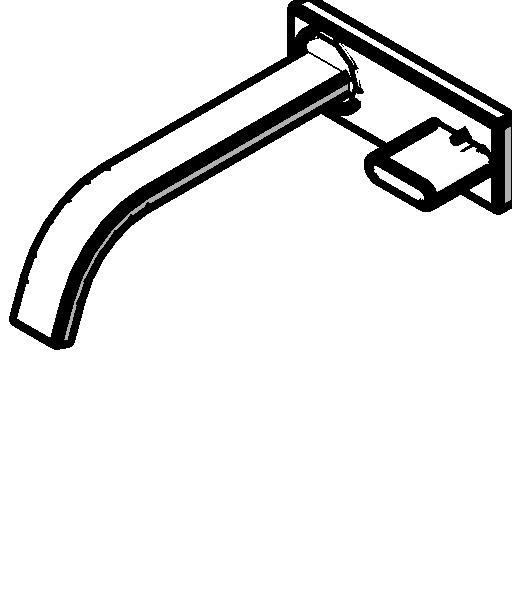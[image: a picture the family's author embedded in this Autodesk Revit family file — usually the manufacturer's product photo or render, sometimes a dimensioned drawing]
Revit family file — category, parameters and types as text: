
# Revit family: Deca_Torneira de parede com chapa para lavatório_Polo_1179.33
name_source: partatom
category: Plumbing Fixtures
units: mm (PartAtom-declared; Revit-internal decimal feet)

## family parameters
Cut with Voids When Loaded = No
Host = Face
Part Type = Normal
Room Calculation Point = No
Round Connector Dimension = Use Radius
Shared = No

## types (4) — shared parameters
Acompanha o Produto = Acompanha Deca confort
Aprovado por = quattroD
Atendimento ao Cliente = 0800-0117073
Categoria = METAIS PARA BANHEIRO
Composição Anel Vedação = -
Composição Assento = -
Composição Básica = Liga de Cobre (bronze e latão),Plásticos de Engenharia,Elastômeros
Composição Componente = -
Consumo = -
Cor Interna = -
Cor Secundária = -
Cores Componente = -
Criado por = quattroD
Código Pai = 1179.33
Default Elevation = 1100 mm
Description = Torneira de parede com chapa para lavatório
Diâmetro Água Fria = 15 mm  [stored 0.0492126 ft]
Informações Complementares = -
Itens de Instalação = -
Linha = Polo
Manufacturer = Deca
Norma = NBR10281
Pressão máx. funcionamento = 40 MCA
Pressão mín. Aquec. Acúmulo = -
Pressão mín. Aquec. Passagem = -
Pressão mín. funcionamento = 2 MCA
Raio Água Fria = 8 mm  [stored 0.0262467 ft]
Saída de Esgoto = -
Segmento = Banheiro Médio
Tipo de dispositivo economizador = Sim
Tipo de mecanismo utilizado = MVC -1/4 volta
Tipo de rosca de entrada = BSP NBR 8133
Tipo de rosca de saída = -
URL = www.deca.com.br
Vazão na Pressão máx. (L/min) = 6
Vazão na Pressão mín. (L/min) = 4
zero-valued in all types: CWFU

## per-type parameters (varying)
| type | Cor Principal | Material | Model | Peso Líquido (Kg) |
| 1179.C33_Cromado | Cromado | Deca_Cromado | 1179.C33 | 1.465 |
| 1179.GL33_Gold | Gold | Deca_Gold | 1179.GL33 | 1.61 |
| 1179.BL33.NO_Black Noir | Black Noir | Deca_Black Noir | 1179.BL33.NO | 1.656 |
| 1179.GL33.RD_Red Gold | Red Gold | Deca_Red Gold | 1179.GL33.RD | 1.465 |

note: source unit labels omitted for Vazão na Pressão máx. (L/min), Vazão na Pressão mín. (L/min) — the stored unit's dimension contradicts the parameter name (converter mislabeling)

note: [stored X ft] marks values corroborated as IEEE doubles in the binary element streams (Revit-internal decimal feet)

## geometry (parser evidence)
native form markers: Sweep x4
no freeform markers — native parametric forms only
